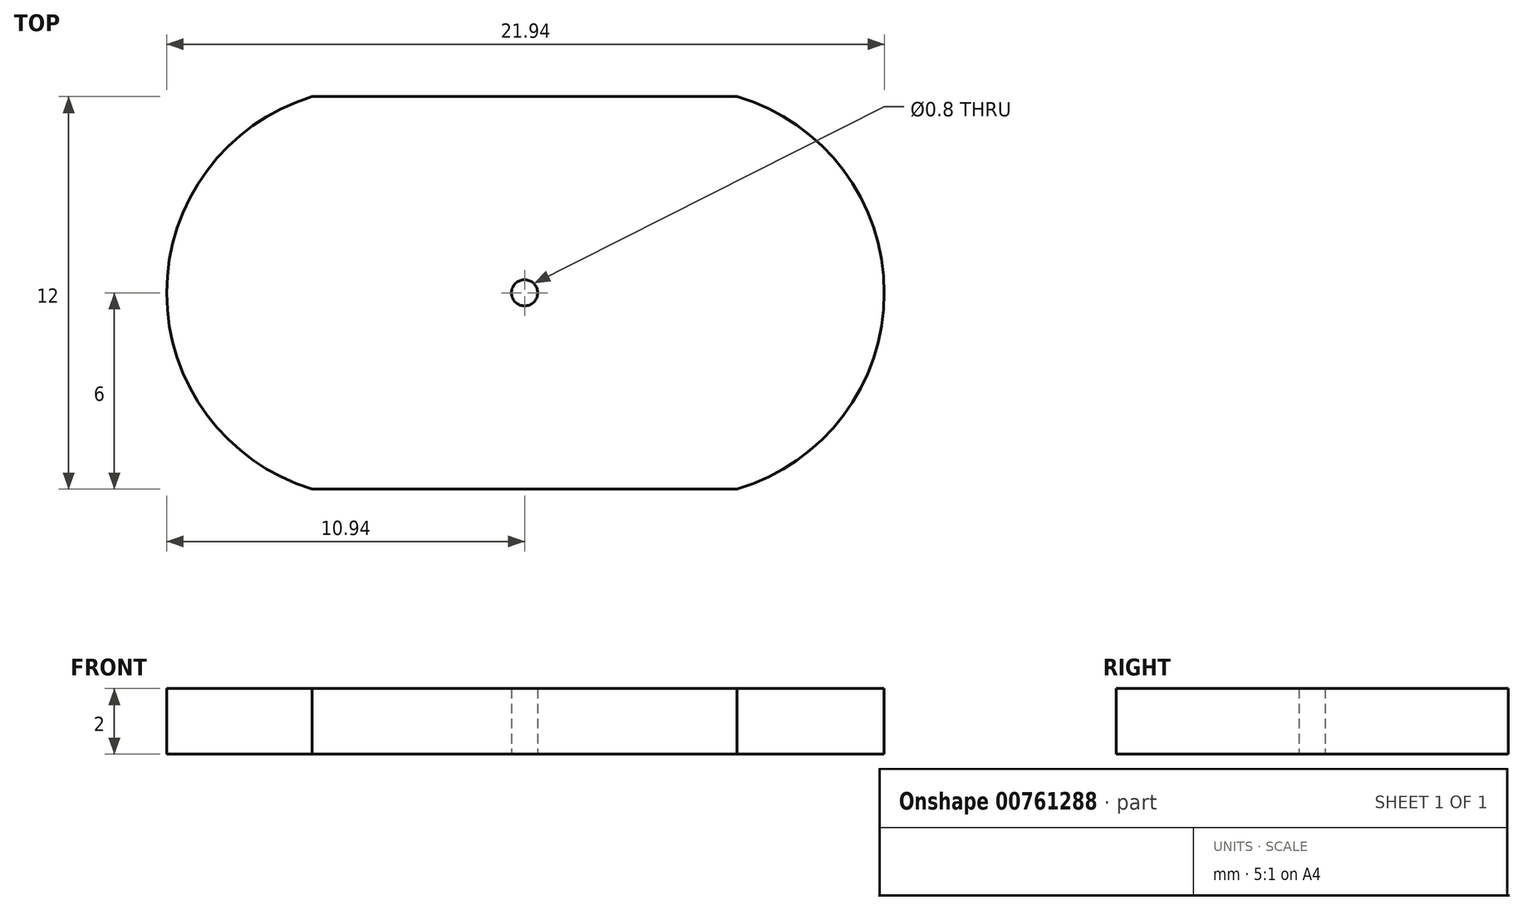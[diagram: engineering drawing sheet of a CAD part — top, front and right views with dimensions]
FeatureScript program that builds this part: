
annotation { "Feature Type Name" : "Feature", "Feature Type Description" : "" }
export const myFeature = defineFeature(function(context is Context, id is Id, definition is map)
    precondition{}
    {
        {
            var Q0;
            Q0=qCreatedBy(makeId("Top.planeOp"),FACE);
            var sketch = newSketch(context, id + "F0", { "sketchPlane" : qUnion([Q0])});
            skLineSegment(sketch, "E0.bottom", {"start": v(6.5, -6) * mm, "end": v(-6.5, -6) * mm});
            skLineSegment(sketch, "E0.top", {"start": v(6.5, 6) * mm, "end": v(-6.5, 6) * mm});
            skPoint(sketch, "E0.middle", {"position": v(0, 0) * mm});
            skLineSegment(sketch, "E1", {"start": v(-11, 7.8) * mm, "end": v(-11, -7.92) * mm, "construction": true});
            skLineSegment(sketch, "E2", {"start": v(11, 7.83) * mm, "end": v(11, -8.37) * mm, "construction": true});
            skArc(sketch, "E3", {"start": v(-6.5, 6) * mm, "mid": v(-10.94, 0) * mm, "end": v(-6.5, -6) * mm});
            skArc(sketch, "E4", {"start": v(6.5, -6) * mm, "mid": v(11, 0) * mm, "end": v(6.5, 6) * mm});
            skCircle(sketch, "E5", {"center": v(0, 0) * mm, "radius": 0.4 * mm});
            skSolve(sketch);
        }
        {
            var Q0;
            Q0=makeQuery(id+"F0.imprint","IMPRINT",FACE,{"disambiguationData":[TD([[makeQuery(id+"F0.imprint","IMPRINT",EDGE,{"derivedFrom":sQuery(id+"F0.wireOp",EDGE,"E0.bottom")}),-1.0]])]});
            extrude(context, id + "F1", {"entities" : qUnion([Q0]), "depth" : 2 * mm, "offsetDistance" : 25 * mm});
        }
    });
